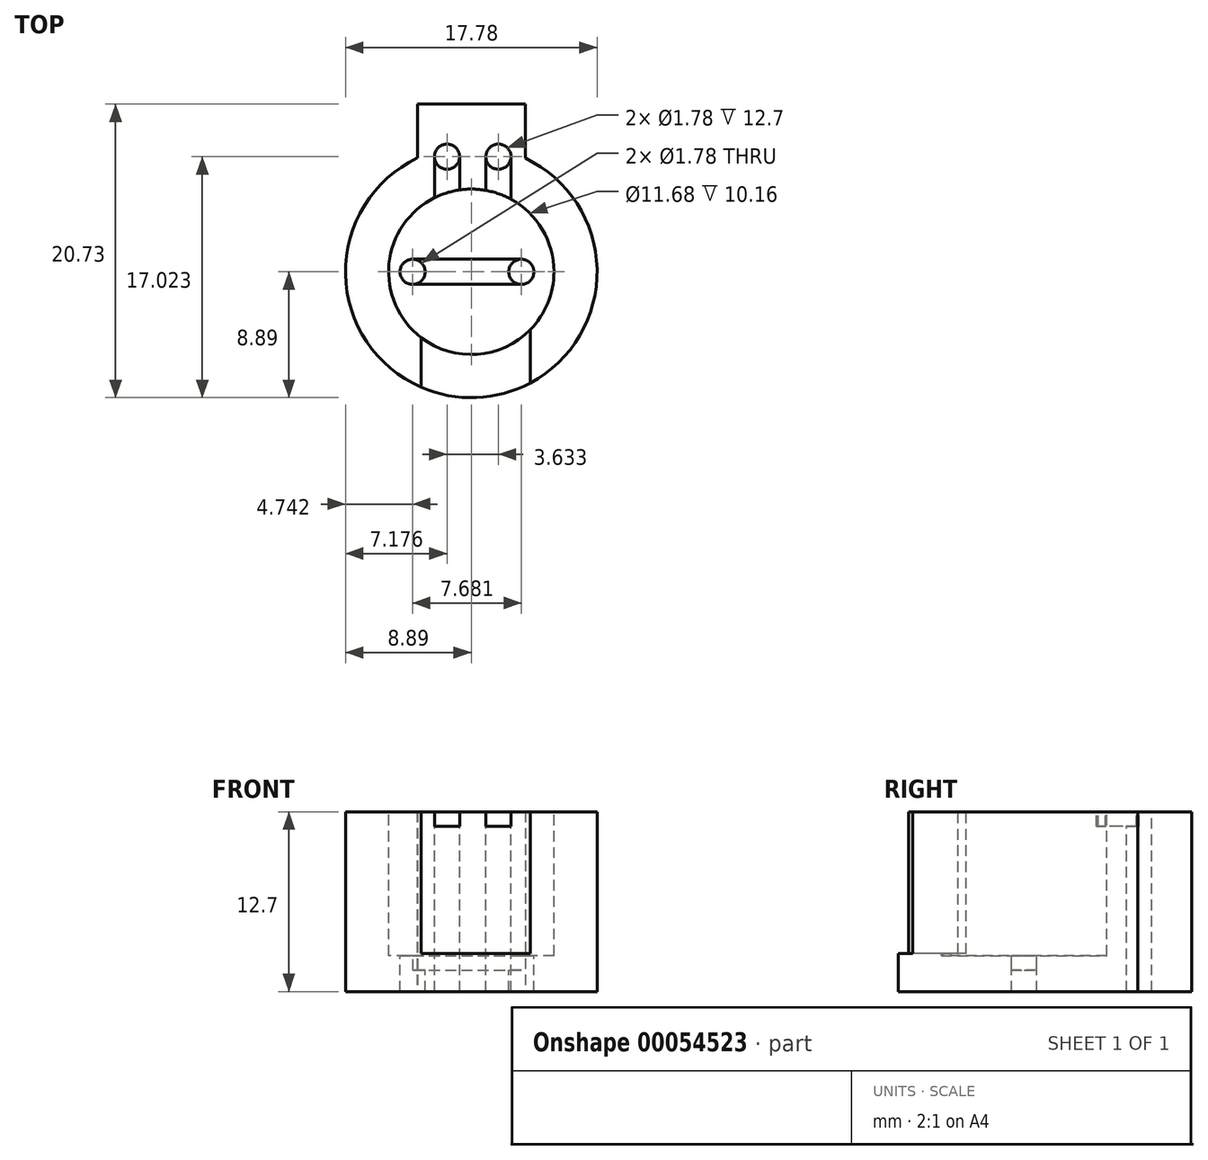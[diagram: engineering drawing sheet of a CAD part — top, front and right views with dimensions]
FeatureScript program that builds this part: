
annotation { "Feature Type Name" : "Feature", "Feature Type Description" : "" }
export const myFeature = defineFeature(function(context is Context, id is Id, definition is map)
    precondition{}
    {
        {
            var Q0;
            Q0=qCreatedBy(makeId("Top.planeOp"),FACE);
            var sketch = newSketch(context, id + "F0", { "sketchPlane" : qUnion([Q0])});
            skCircle(sketch, "E0", {"center": v(0, 0) * mm, "radius": 7.62 * mm});
            skArc(sketch, "E1.0", {"start": v(-3.82, 8.03) * mm, "mid": v(0, -8.89) * mm, "end": v(3.82, 8.03) * mm});
            skLineSegment(sketch, "E2.bottom", {"start": v(-3.8, 11.84) * mm, "end": v(3.82, 11.84) * mm});
            skLineSegment(sketch, "E2.top", {"start": v(-3.82, 8.03) * mm, "end": v(-3.8, 8.03) * mm});
            skLineSegment(sketch, "E2.left", {"start": v(-3.8, 11.84) * mm, "end": v(-3.8, 8.03) * mm});
            skLineSegment(sketch, "E2.right", {"start": v(3.82, 11.84) * mm, "end": v(3.82, 8.03) * mm});
            skSolve(sketch);
        }
        {
            var Q0;
            Q0=makeQuery(id+"F0.imprint","IMPRINT",FACE,{"disambiguationData":[TD([[makeQuery(id+"F0.imprint","IMPRINT",EDGE,{"derivedFrom":sQuery(id+"F0.wireOp",EDGE,"E0")}),1.0]])]});
            var Q1;
            Q1=makeQuery(id+"F0.imprint","IMPRINT",FACE,{"disambiguationData":[TD([[makeQuery(id+"F0.imprint","IMPRINT",EDGE,{"derivedFrom":sQuery(id+"F0.wireOp",EDGE,"E0")}),-1.0]])]});
            extrude(context, id + "F1", {"entities" : qUnion([Q0, Q1]), "depth" : 12.7 * mm});
        }
        {
            var Q0;
            Q0=makeQuery(id+"F1.opExtrude","CAP_FACE",FACE,{"disambiguationData":[OSD([sQuery(id+"F0.wireOp",EDGE,"E1.0"),sQuery(id+"F0.wireOp",EDGE,"E2.bottom"),sQuery(id+"F0.wireOp",EDGE,"E2.top"),sQuery(id+"F0.wireOp",EDGE,"E2.left"),sQuery(id+"F0.wireOp",EDGE,"E2.right")])],"isStart":false});
            var sketch = newSketch(context, id + "F2", { "sketchPlane" : qUnion([Q0])});
            skCircle(sketch, "E3", {"center": v(0, 0) * mm, "radius": 5.84 * mm});
            skSolve(sketch);
        }
        {
            var Q0;
            Q0=makeQuery(id+"F2.imprint","IMPRINT",FACE,{"disambiguationData":[TD([[makeQuery(id+"F2.imprint","IMPRINT",EDGE,{"derivedFrom":sQuery(id+"F2.wireOp",EDGE,"E3")}),1.0]])]});
            extrude(context, id + "F3", {"entities" : qUnion([Q0]), "operationType" : NewBodyOperationType.REMOVE, "oppositeDirection" : true, "depth" : 10.16 * mm});
        }
        {
            var Q0;
            Q0=makeQuery(id+"F1.opExtrude","CAP_FACE",FACE,{"disambiguationData":[OSD([sQuery(id+"F0.wireOp",EDGE,"E1.0"),sQuery(id+"F0.wireOp",EDGE,"E2.bottom"),sQuery(id+"F0.wireOp",EDGE,"E2.top"),sQuery(id+"F0.wireOp",EDGE,"E2.left"),sQuery(id+"F0.wireOp",EDGE,"E2.right")])],"isStart":false});
            var sketch = newSketch(context, id + "F4", { "sketchPlane" : qUnion([Q0])});
            skCircle(sketch, "E4", {"center": v(-1.71, 8.13) * mm, "radius": 0.89 * mm});
            skCircle(sketch, "E5", {"center": v(1.92, 8.13) * mm, "radius": 0.89 * mm});
            skSolve(sketch);
        }
        {
            var Q0;
            Q0=makeQuery(id+"F4.imprint","IMPRINT",FACE,{"disambiguationData":[TD([[makeQuery(id+"F4.imprint","IMPRINT",EDGE,{"derivedFrom":sQuery(id+"F4.wireOp",EDGE,"E4")}),1.0]])]});
            var Q1;
            Q1=makeQuery(id+"F4.imprint","IMPRINT",FACE,{"disambiguationData":[TD([[makeQuery(id+"F4.imprint","IMPRINT",EDGE,{"derivedFrom":sQuery(id+"F4.wireOp",EDGE,"E5")}),1.0]])]});
            extrude(context, id + "F5", {"entities" : qUnion([Q0, Q1]), "operationType" : NewBodyOperationType.REMOVE, "oppositeDirection" : true, "depth" : 25.4 * mm});
        }
        {
            var Q0;
            Q0=makeQuery(id+"F1.opExtrude","CAP_FACE",FACE,{"disambiguationData":[OSD([sQuery(id+"F0.wireOp",EDGE,"E1.0"),sQuery(id+"F0.wireOp",EDGE,"E2.bottom"),sQuery(id+"F0.wireOp",EDGE,"E2.top"),sQuery(id+"F0.wireOp",EDGE,"E2.left"),sQuery(id+"F0.wireOp",EDGE,"E2.right")])],"isStart":false});
            var sketch = newSketch(context, id + "F6", { "sketchPlane" : qUnion([Q0])});
            skLineSegment(sketch, "E6", {"start": v(-2.58, 7.95) * mm, "end": v(-2.58, 5.24) * mm});
            skLineSegment(sketch, "E7", {"start": v(-0.82, 8.14) * mm, "end": v(-0.82, 5.78) * mm});
            skLineSegment(sketch, "E8", {"start": v(1.03, 8.14) * mm, "end": v(1.03, 5.75) * mm});
            skLineSegment(sketch, "E9", {"start": v(2.8, 8.08) * mm, "end": v(2.8, 5.12) * mm});
            skSolve(sketch);
        }
        {
            var Q0;
            {var subQ0=sQuery(id+"F6.wireOp",EDGE,"E6");Q0=makeQuery(id+"F6.imprint","IMPRINT",FACE,{"disambiguationData":[TD([[makeQuery(id+"F6.imprint","IMPRINT",EDGE,{"derivedFrom":subQ0}),1.0]])]});}
            var Q1;
            {var subQ5=sQuery(id+"F6.wireOp",EDGE,"E9");Q1=makeQuery(id+"F6.imprint","IMPRINT",FACE,{"disambiguationData":[TD([[makeQuery(id+"F6.imprint","IMPRINT",EDGE,{"derivedFrom":subQ5}),-1.0]])]});}
            extrude(context, id + "F7", {"entities" : qUnion([Q0, Q1]), "operationType" : NewBodyOperationType.REMOVE, "oppositeDirection" : true, "depth" : 1.02 * mm});
        }
        {
            var Q0;
            Q0=makeQuery(id+"F3.boolean.opBoolean","COPY",FACE,{"derivedFrom":makeQuery(id+"F3.opExtrude","CAP_FACE",FACE,{"disambiguationData":[OSD([sQuery(id+"F2.wireOp",EDGE,"E3")])],"isStart":false})});
            var sketch = newSketch(context, id + "F8", { "sketchPlane" : qUnion([Q0])});
            skCircle(sketch, "E10", {"center": v(-4.15, 0) * mm, "radius": 0.89 * mm});
            skCircle(sketch, "E11", {"center": v(3.53, 0) * mm, "radius": 0.89 * mm});
            skSolve(sketch);
        }
        {
            var Q0;
            Q0=makeQuery(id+"F8.imprint","IMPRINT",FACE,{"disambiguationData":[TD([[makeQuery(id+"F8.imprint","IMPRINT",EDGE,{"derivedFrom":sQuery(id+"F8.wireOp",EDGE,"E10")}),1.0]])]});
            var Q1;
            Q1=makeQuery(id+"F8.imprint","IMPRINT",FACE,{"disambiguationData":[TD([[makeQuery(id+"F8.imprint","IMPRINT",EDGE,{"derivedFrom":sQuery(id+"F8.wireOp",EDGE,"E11")}),1.0]])]});
            extrude(context, id + "F9", {"entities" : qUnion([Q0, Q1]), "operationType" : NewBodyOperationType.REMOVE, "oppositeDirection" : true, "depth" : 25.4 * mm});
        }
        {
            var Q0;
            Q0=makeQuery(id+"F3.boolean.opBoolean","COPY",FACE,{"derivedFrom":makeQuery(id+"F3.opExtrude","CAP_FACE",FACE,{"disambiguationData":[OSD([sQuery(id+"F2.wireOp",EDGE,"E3")])],"isStart":false})});
            var sketch = newSketch(context, id + "F10", { "sketchPlane" : qUnion([Q0])});
            skLineSegment(sketch, "E12", {"start": v(-4.12, 0.89) * mm, "end": v(3.53, 0.89) * mm});
            skLineSegment(sketch, "E13", {"start": v(-4.14, -0.89) * mm, "end": v(3.53, -0.89) * mm});
            skSolve(sketch);
        }
        {
            var Q0;
            {var subQ0=sQuery(id+"F10.wireOp",EDGE,"E12");Q0=makeQuery(id+"F10.imprint","IMPRINT",FACE,{"disambiguationData":[TD([[makeQuery(id+"F10.imprint","IMPRINT",EDGE,{"derivedFrom":subQ0}),-1.0]])]});}
            extrude(context, id + "F11", {"entities" : qUnion([Q0]), "operationType" : NewBodyOperationType.REMOVE, "oppositeDirection" : true, "depth" : 1.02 * mm});
        }
        {
            var Q0;
            Q0=qCreatedBy(makeId("Front.planeOp"),FACE);
            cPlane(context, id + "F12", {"entities" : qUnion([Q0]), "cplaneType" : CPlaneType.OFFSET, "offset" : 8.9 * mm, "width" : 152.4 * mm, "height" : 152.4 * mm});
        }
        {
            var Q0;
            Q0=qCreatedBy(id+"F12.planeOp",FACE);
            var sketch = newSketch(context, id + "F13", { "sketchPlane" : qUnion([Q0])});
            skLineSegment(sketch, "E14.bottom", {"start": v(-3.54, 13.2) * mm, "end": v(4.17, 13.2) * mm});
            skLineSegment(sketch, "E14.top", {"start": v(-3.54, 2.68) * mm, "end": v(4.17, 2.68) * mm});
            skLineSegment(sketch, "E14.left", {"start": v(-3.54, 13.2) * mm, "end": v(-3.54, 2.68) * mm});
            skLineSegment(sketch, "E14.right", {"start": v(4.17, 13.2) * mm, "end": v(4.17, 2.68) * mm});
            skSolve(sketch);
        }
        {
            var Q0;
            Q0=makeQuery(id+"F13.imprint","IMPRINT",FACE,{"disambiguationData":[TD([[makeQuery(id+"F13.imprint","IMPRINT",EDGE,{"derivedFrom":sQuery(id+"F13.wireOp",EDGE,"E14.bottom")}),-1.0]])]});
            extrude(context, id + "F14", {"entities" : qUnion([Q0]), "operationType" : NewBodyOperationType.REMOVE, "oppositeDirection" : true, "depth" : 5.08 * mm});
        }
    });
